# Revit family: Sanitary_Bidets_Sanindusa_Urby-Plus_Bidet-With-Hole-For-Water-Supply
name_source: partatom
category: Plumbing Fixtures
revit_build: Autodesk Revit 2018 (Build: 20170223_1515(x64)
units: mm (PartAtom-declared; Revit-internal decimal feet)

## family parameters
Cut with Voids When Loaded = No
Host = Face
Part Type = Normal
Room Calculation Point = No
Round Connector Dimension = Use Diameter
Shared = No

## types (1)
- Sanitary_Bidets_Sanindusa_Urby-Plus_Bidet-With-Hole-For-Water-Supply
    AssetType = Fixed
    BIMObjectName = Bidet_Urby_plus
    BidetMounting = pedestal
    Category = Pr_40_20_06_11,Bidets
    CodePerformance = EN 14528:2007 - CL 25; EN 35:2014
    Color = White
    Constituents = 48011-chromed embellishment ring (included);
    Default Elevation = 1219 mm
    Description = Waste water appliance for washing the excretory organs while sitting astride the bowl (BS6100)
    DrainSize = 47 mm  [stored 0.154199 ft]
    Element Type = BIDET: Waste water appliance for washing the excretory organs while sitting astride the bowl (BS6100)
    Features = "Back to wall bidet, easy to clean. Domestic and hotel use. With hole for one tap
"
    Finish = Gloss
    Installation Instructions = https://www.tec.sanindusa.pt
    InstallationDate = 1900-12-31T23:59:59
    Manufacturer = Sanindusa
    ManufacturerName = Sanindusa
    ManufacturerURL = http://www.sanindusa.pt
    Material = Vitreous China
    Model = 146410004
    ModelNumber = 146410004
    ModelReference = Urb.y Plus
    Name = Bidet_Urb.y Plus
    NominalHeight = 400 mm  [stored 1.31234 ft]
    NominalLength = 345 mm  [stored 1.13189 ft]
    NominalWidth = 475 mm  [stored 1.5584 ft]
    Pre-defined type (IFC) = BIDET
    ProductInformation = https://www.tec.sanindusa.pt
    ProductionYear = 2019
    Size = 345x475x400
    SpilloverLevel = 114
    Type (IFC) = IfcSanitaryTerminalType
    URL = www.tec.sanindusa.pt
    Uniclass2015Code = Pr_40_20_06_11
    Uniclass2015Title = Bidets
    Uniclass2015Version = Products v1.6
    Version = 1
    WarrantyDescription = https://www.tec.sanindusa.pt
    WarrantyDurationParts = 5
    WarrantyDurationUnit = year
    WarrantyStartDate = 1900-12-31T23:59:59
    Waste Connection = Yes
    Weight = 26.95 kg

note: [stored X ft] marks values corroborated as IEEE doubles in the binary element streams (Revit-internal decimal feet)

## geometry (parser evidence)
native form markers: Sweep x6
no freeform markers — native parametric forms only
